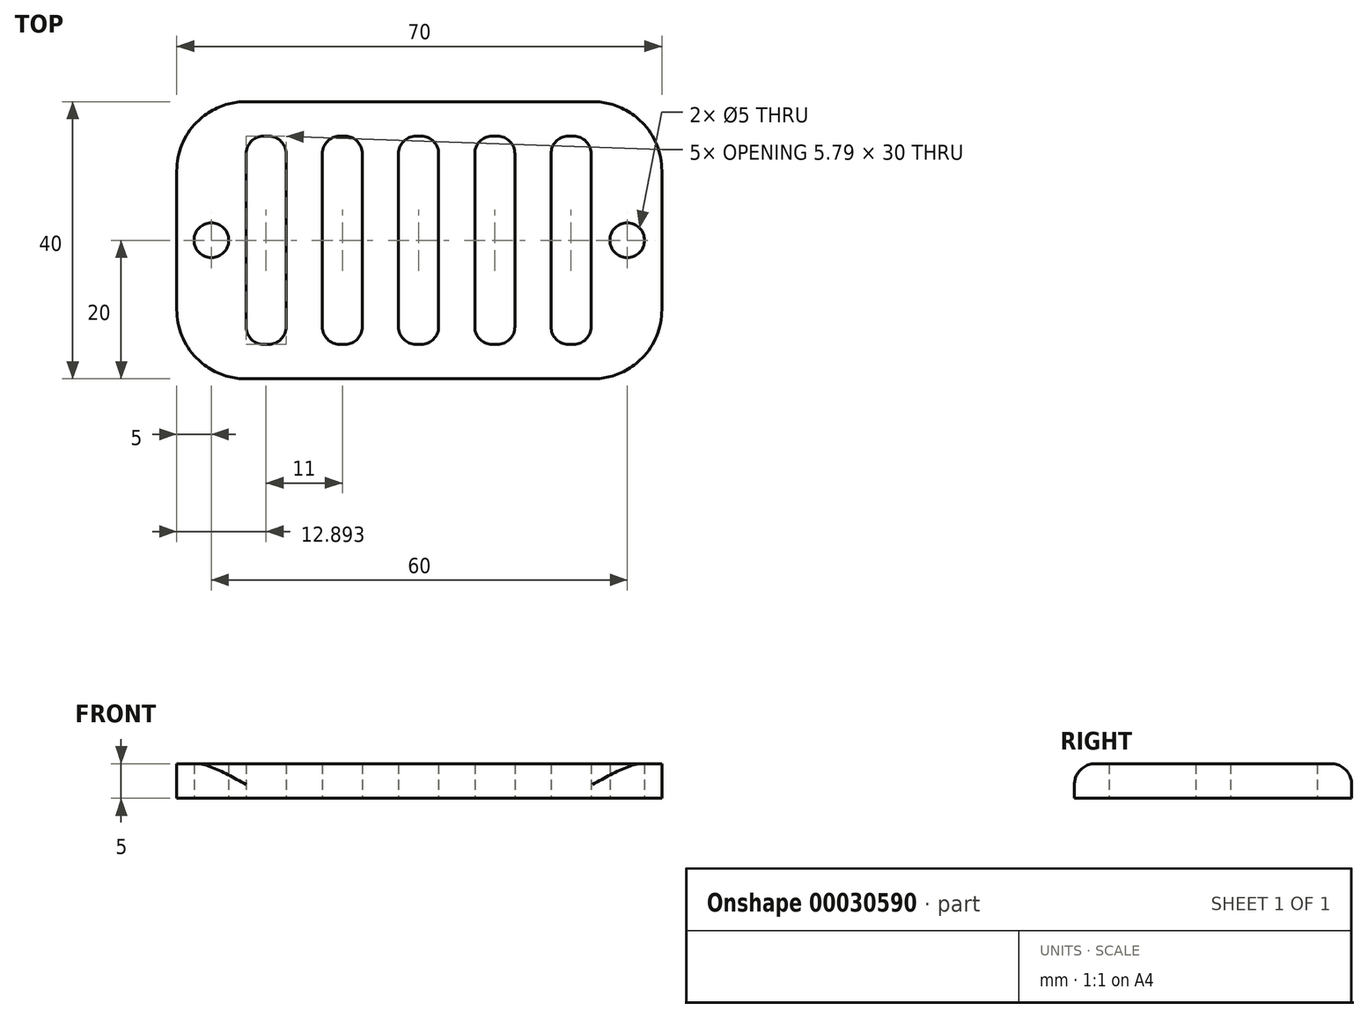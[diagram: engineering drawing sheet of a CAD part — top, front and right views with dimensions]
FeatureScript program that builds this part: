
annotation { "Feature Type Name" : "Feature", "Feature Type Description" : "" }
export const myFeature = defineFeature(function(context is Context, id is Id, definition is map)
    precondition{}
    {
        {
            var Q0;
            Q0=qCreatedBy(makeId("Top.planeOp"),FACE);
            var sketch = newSketch(context, id + "F0", { "sketchPlane" : qUnion([Q0])});
            skLineSegment(sketch, "E0.rect.bottom", {"start": v(-35, 20) * mm, "end": v(35, 20) * mm});
            skLineSegment(sketch, "E0.rect.top", {"start": v(-35, -20) * mm, "end": v(35, -20) * mm});
            skLineSegment(sketch, "E0.rect.left", {"start": v(-35, 20) * mm, "end": v(-35, -20) * mm});
            skLineSegment(sketch, "E0.rect.right", {"start": v(35, 20) * mm, "end": v(35, -20) * mm});
            skPoint(sketch, "E0.rect.middle", {"position": v(0, 0) * mm});
            skCircle(sketch, "E1", {"center": v(-30, 0) * mm, "radius": 2.5 * mm});
            skCircle(sketch, "E2", {"center": v(30, 0) * mm, "radius": 2.5 * mm});
            skLineSegment(sketch, "E3.rect.bottom", {"start": v(-22.5, 15) * mm, "end": v(-21.71, 15) * mm});
            skLineSegment(sketch, "E3.rect.top", {"start": v(-22.5, -15) * mm, "end": v(-21.71, -15) * mm});
            skLineSegment(sketch, "E3.rect.left", {"start": v(-25, 12.5) * mm, "end": v(-25, -12.5) * mm});
            skLineSegment(sketch, "E3.rect.right", {"start": v(-19.21, 12.5) * mm, "end": v(-19.21, -12.5) * mm});
            skPoint(sketch, "E3.rect.middle", {"position": v(-22.1, 0) * mm});
            skPoint(sketch, "E4.visualSharp", {"position": v(-19.21, 15) * mm});
            skArc(sketch, "E4.filletArc", {"start": v(-19.21, 12.5) * mm, "mid": v(-19.95, 14.27) * mm, "end": v(-21.71, 15) * mm});
            skPoint(sketch, "E5.visualSharp", {"position": v(-25, 15) * mm});
            skArc(sketch, "E5.filletArc", {"start": v(-22.5, 15) * mm, "mid": v(-24.27, 14.27) * mm, "end": v(-25, 12.5) * mm});
            skPoint(sketch, "E6.visualSharp", {"position": v(-25, -15) * mm});
            skArc(sketch, "E6.filletArc", {"start": v(-25, -12.5) * mm, "mid": v(-24.27, -14.27) * mm, "end": v(-22.5, -15) * mm});
            skPoint(sketch, "E7.visualSharp", {"position": v(-19.21, -15) * mm});
            skArc(sketch, "E7.filletArc", {"start": v(-21.71, -15) * mm, "mid": v(-19.95, -14.27) * mm, "end": v(-19.21, -12.5) * mm});
            skPoint(sketch, "E8.1.0.0", {"position": v(-14, -15) * mm});
            skPoint(sketch, "E8.1.0.1", {"position": v(-8.21, -15) * mm});
            skLineSegment(sketch, "E8.1.0.2", {"start": v(-14, 12.5) * mm, "end": v(-14, -12.5) * mm});
            skLineSegment(sketch, "E8.1.0.3", {"start": v(-8.21, 12.5) * mm, "end": v(-8.21, -12.5) * mm});
            skPoint(sketch, "E8.1.0.4", {"position": v(-11.1, 0) * mm});
            skPoint(sketch, "E8.1.0.5", {"position": v(-8.21, 15) * mm});
            skPoint(sketch, "E8.1.0.6", {"position": v(-14, 15) * mm});
            skArc(sketch, "E8.1.0.7", {"start": v(-11.5, 15) * mm, "mid": v(-13.27, 14.27) * mm, "end": v(-14, 12.5) * mm});
            skArc(sketch, "E8.1.0.8", {"start": v(-8.21, 12.5) * mm, "mid": v(-8.95, 14.27) * mm, "end": v(-10.71, 15) * mm});
            skArc(sketch, "E8.1.0.9", {"start": v(-14, -12.5) * mm, "mid": v(-13.27, -14.27) * mm, "end": v(-11.5, -15) * mm});
            skArc(sketch, "E8.1.0.10", {"start": v(-10.71, -15) * mm, "mid": v(-8.95, -14.27) * mm, "end": v(-8.21, -12.5) * mm});
            skLineSegment(sketch, "E8.1.0.11", {"start": v(-11.5, 15) * mm, "end": v(-10.71, 15) * mm});
            skLineSegment(sketch, "E8.1.0.12", {"start": v(-11.5, -15) * mm, "end": v(-10.71, -15) * mm});
            skPoint(sketch, "E8.2.0.0", {"position": v(-3, -15) * mm});
            skPoint(sketch, "E8.2.0.1", {"position": v(2.79, -15) * mm});
            skLineSegment(sketch, "E8.2.0.2", {"start": v(-3, 12.5) * mm, "end": v(-3, -12.5) * mm});
            skLineSegment(sketch, "E8.2.0.3", {"start": v(2.79, 12.5) * mm, "end": v(2.79, -12.5) * mm});
            skPoint(sketch, "E8.2.0.4", {"position": v(-0.1, 0) * mm});
            skPoint(sketch, "E8.2.0.5", {"position": v(2.79, 15) * mm});
            skPoint(sketch, "E8.2.0.6", {"position": v(-3, 15) * mm});
            skArc(sketch, "E8.2.0.7", {"start": v(-0.5, 15) * mm, "mid": v(-2.27, 14.27) * mm, "end": v(-3, 12.5) * mm});
            skArc(sketch, "E8.2.0.8", {"start": v(2.79, 12.5) * mm, "mid": v(2.05, 14.27) * mm, "end": v(0.29, 15) * mm});
            skArc(sketch, "E8.2.0.9", {"start": v(-3, -12.5) * mm, "mid": v(-2.27, -14.27) * mm, "end": v(-0.5, -15) * mm});
            skArc(sketch, "E8.2.0.10", {"start": v(0.29, -15) * mm, "mid": v(2.05, -14.27) * mm, "end": v(2.79, -12.5) * mm});
            skLineSegment(sketch, "E8.2.0.11", {"start": v(-0.5, 15) * mm, "end": v(0.29, 15) * mm});
            skLineSegment(sketch, "E8.2.0.12", {"start": v(-0.5, -15) * mm, "end": v(0.29, -15) * mm});
            skPoint(sketch, "E8.3.0.0", {"position": v(8, -15) * mm});
            skPoint(sketch, "E8.3.0.1", {"position": v(13.79, -15) * mm});
            skLineSegment(sketch, "E8.3.0.2", {"start": v(8, 12.5) * mm, "end": v(8, -12.5) * mm});
            skLineSegment(sketch, "E8.3.0.3", {"start": v(13.79, 12.5) * mm, "end": v(13.79, -12.5) * mm});
            skPoint(sketch, "E8.3.0.4", {"position": v(10.9, 0) * mm});
            skPoint(sketch, "E8.3.0.5", {"position": v(13.79, 15) * mm});
            skPoint(sketch, "E8.3.0.6", {"position": v(8, 15) * mm});
            skArc(sketch, "E8.3.0.7", {"start": v(10.5, 15) * mm, "mid": v(8.73, 14.27) * mm, "end": v(8, 12.5) * mm});
            skArc(sketch, "E8.3.0.8", {"start": v(13.79, 12.5) * mm, "mid": v(13.05, 14.27) * mm, "end": v(11.29, 15) * mm});
            skArc(sketch, "E8.3.0.9", {"start": v(8, -12.5) * mm, "mid": v(8.73, -14.27) * mm, "end": v(10.5, -15) * mm});
            skArc(sketch, "E8.3.0.10", {"start": v(11.29, -15) * mm, "mid": v(13.05, -14.27) * mm, "end": v(13.79, -12.5) * mm});
            skLineSegment(sketch, "E8.3.0.11", {"start": v(10.5, 15) * mm, "end": v(11.29, 15) * mm});
            skLineSegment(sketch, "E8.3.0.12", {"start": v(10.5, -15) * mm, "end": v(11.29, -15) * mm});
            skPoint(sketch, "E8.4.0.0", {"position": v(19, -15) * mm});
            skPoint(sketch, "E8.4.0.1", {"position": v(24.79, -15) * mm});
            skLineSegment(sketch, "E8.4.0.2", {"start": v(19, 12.5) * mm, "end": v(19, -12.5) * mm});
            skLineSegment(sketch, "E8.4.0.3", {"start": v(24.79, 12.5) * mm, "end": v(24.79, -12.5) * mm});
            skPoint(sketch, "E8.4.0.4", {"position": v(21.9, 0) * mm});
            skPoint(sketch, "E8.4.0.5", {"position": v(24.79, 15) * mm});
            skPoint(sketch, "E8.4.0.6", {"position": v(19, 15) * mm});
            skArc(sketch, "E8.4.0.7", {"start": v(21.5, 15) * mm, "mid": v(19.73, 14.27) * mm, "end": v(19, 12.5) * mm});
            skArc(sketch, "E8.4.0.8", {"start": v(24.79, 12.5) * mm, "mid": v(24.05, 14.27) * mm, "end": v(22.29, 15) * mm});
            skArc(sketch, "E8.4.0.9", {"start": v(19, -12.5) * mm, "mid": v(19.73, -14.27) * mm, "end": v(21.5, -15) * mm});
            skArc(sketch, "E8.4.0.10", {"start": v(22.29, -15) * mm, "mid": v(24.05, -14.27) * mm, "end": v(24.79, -12.5) * mm});
            skLineSegment(sketch, "E8.4.0.11", {"start": v(21.5, 15) * mm, "end": v(22.29, 15) * mm});
            skLineSegment(sketch, "E8.4.0.12", {"start": v(21.5, -15) * mm, "end": v(22.29, -15) * mm});
            skLineSegment(sketch, "E8.direction1", {"start": v(-25, -15) * mm, "end": v(-14, -15) * mm, "construction": true});
            skSolve(sketch);
        }
        {
            var Q0;
            Q0 = qSketchRegion(id + "F0", true);
            extrude(context, id + "F1", {"entities" : qUnion([Q0]), "depth" : 5 * mm});
        }
        {
            var Q0;
            Q0=makeQuery(id+"F1.opExtrude","SWEPT_EDGE",EDGE,{"disambiguationData":[OSD([sQuery(id+"F0.wireOp",EDGE,"E0.rect.bottom"),sQuery(id+"F0.wireOp",EDGE,"E0.rect.left")])]});
            var Q1;
            Q1=makeQuery(id+"F1.opExtrude","SWEPT_EDGE",EDGE,{"disambiguationData":[OSD([sQuery(id+"F0.wireOp",EDGE,"E0.rect.top"),sQuery(id+"F0.wireOp",EDGE,"E0.rect.left")])]});
            var Q2;
            Q2=makeQuery(id+"F1.opExtrude","SWEPT_EDGE",EDGE,{"disambiguationData":[OSD([sQuery(id+"F0.wireOp",EDGE,"E0.rect.top"),sQuery(id+"F0.wireOp",EDGE,"E0.rect.right")])]});
            var Q3;
            Q3=makeQuery(id+"F1.opExtrude","SWEPT_EDGE",EDGE,{"disambiguationData":[OSD([sQuery(id+"F0.wireOp",EDGE,"E0.rect.bottom"),sQuery(id+"F0.wireOp",EDGE,"E0.rect.right")])]});
            fillet(context, id + "F2", {"entities" : qUnion([Q0, Q1, Q2, Q3]), "radius" : 10 * mm, "tangentPropagation" : true, "allowEdgeOverflow" : false});
        }
        {
            var Q0;
            Q0=makeQuery(id+"F1.opExtrude","CAP_EDGE",EDGE,{"disambiguationData":[OSD([sQuery(id+"F0.wireOp",EDGE,"E0.rect.top")])],"isStart":false});
            var Q1;
            Q1=makeQuery(id+"F1.opExtrude","CAP_EDGE",EDGE,{"disambiguationData":[OSD([sQuery(id+"F0.wireOp",EDGE,"E0.rect.bottom")])],"isStart":false});
            fillet(context, id + "F3", {"entities" : qUnion([Q0, Q1]), "radius" : 3 * mm, "allowEdgeOverflow" : false});
        }
    });
